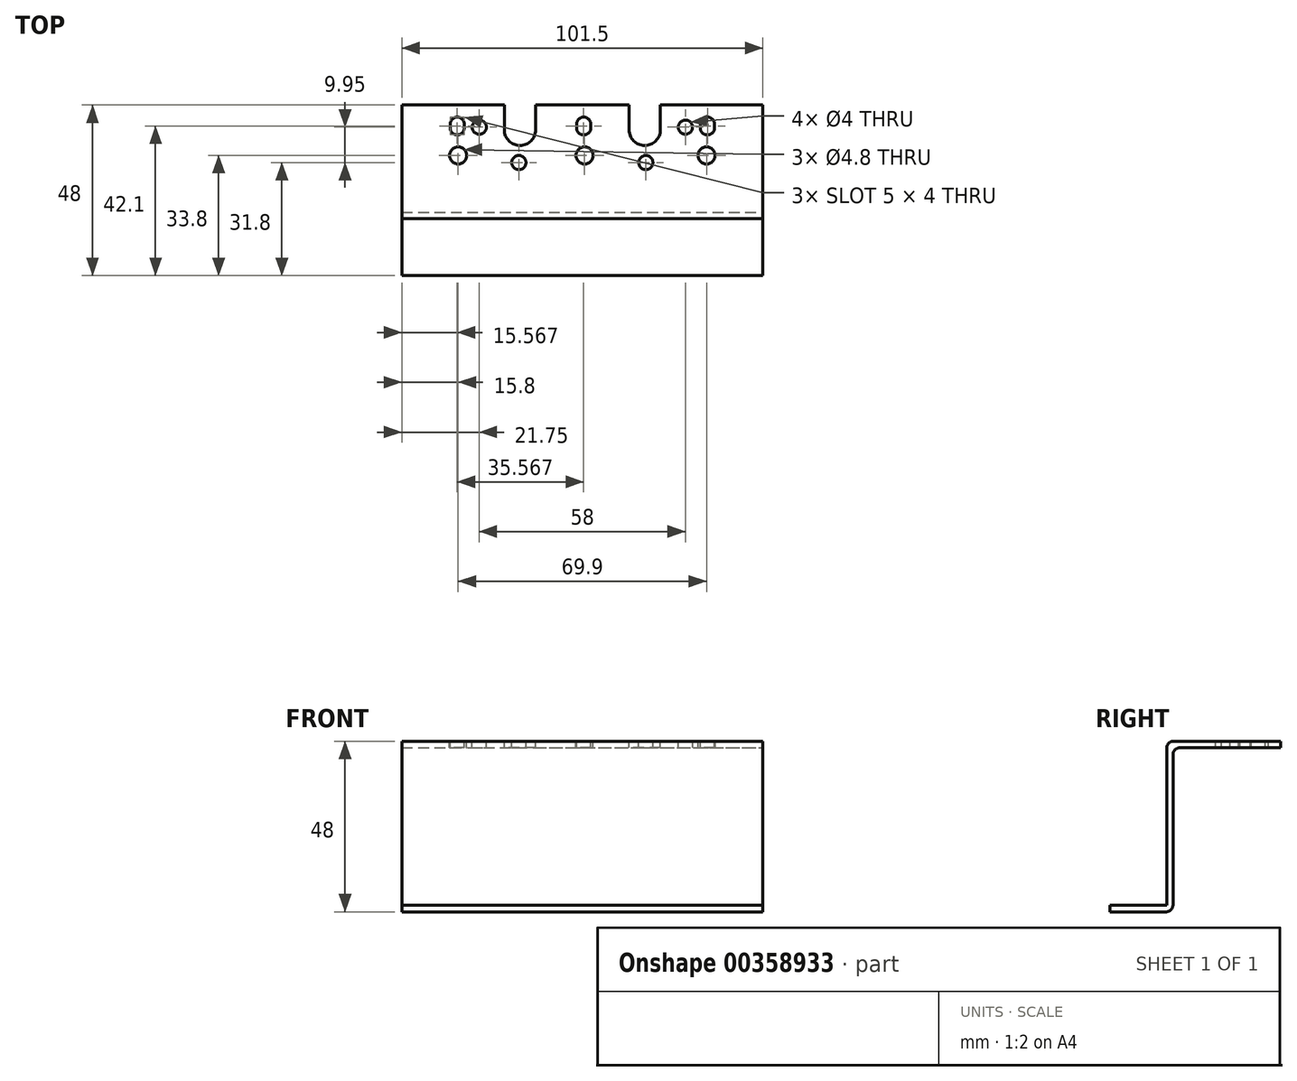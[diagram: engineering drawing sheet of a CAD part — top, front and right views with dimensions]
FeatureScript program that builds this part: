
annotation { "Feature Type Name" : "Feature", "Feature Type Description" : "" }
export const myFeature = defineFeature(function(context is Context, id is Id, definition is map)
    precondition{}
    {
        {
            var Q0;
            Q0=qCreatedBy(makeId("Front.planeOp"),FACE);
            var sketch = newSketch(context, id + "F0", { "sketchPlane" : qUnion([Q0])});
            skLineSegment(sketch, "E0.bottom", {"start": v(0, 0) * mm, "end": v(101.5, 0) * mm});
            skLineSegment(sketch, "E0.top", {"start": v(0, 48) * mm, "end": v(101.5, 48) * mm});
            skLineSegment(sketch, "E0.left", {"start": v(0, 0) * mm, "end": v(0, 48) * mm});
            skLineSegment(sketch, "E0.right", {"start": v(101.5, 0) * mm, "end": v(101.5, 48) * mm});
            skSolve(sketch);
        }
        {
            var Q0;
            Q0 = qSketchRegion(id + "F0", true);
            extrude(context, id + "F1", {"entities" : qUnion([Q0]), "depth" : 1.8 * mm});
        }
        {
            var Q0;
            Q0=makeQuery(id+"F1.opExtrude","CAP_FACE",FACE,{"disambiguationData":[OSD([sQuery(id+"F0.wireOp",EDGE,"E0.bottom"),sQuery(id+"F0.wireOp",EDGE,"E0.top"),sQuery(id+"F0.wireOp",EDGE,"E0.left"),sQuery(id+"F0.wireOp",EDGE,"E0.right")])],"isStart":false});
            var sketch = newSketch(context, id + "F2", { "sketchPlane" : qUnion([Q0])});
            skLineSegment(sketch, "E1.bottom", {"start": v(0, 0) * mm, "end": v(101.5, 0) * mm});
            skLineSegment(sketch, "E1.top", {"start": v(0, 1.8) * mm, "end": v(101.5, 1.8) * mm});
            skLineSegment(sketch, "E1.left", {"start": v(0, 0) * mm, "end": v(0, 1.8) * mm});
            skLineSegment(sketch, "E1.right", {"start": v(101.5, 0) * mm, "end": v(101.5, 1.8) * mm});
            skLineSegment(sketch, "E2.bottom", {"start": v(0, 48) * mm, "end": v(101.5, 48) * mm});
            skLineSegment(sketch, "E2.top", {"start": v(0, 46.2) * mm, "end": v(101.5, 46.2) * mm});
            skLineSegment(sketch, "E2.left", {"start": v(0, 48) * mm, "end": v(0, 46.2) * mm});
            skLineSegment(sketch, "E2.right", {"start": v(101.5, 48) * mm, "end": v(101.5, 46.2) * mm});
            skSolve(sketch);
        }
        {
            var Q0;
            Q0=makeQuery(id+"F2.imprint","IMPRINT",FACE,{"disambiguationData":[TD([[makeQuery(id+"F2.imprint","IMPRINT",EDGE,{"derivedFrom":sQuery(id+"F2.wireOp",EDGE,"E1.bottom")}),1.0]])]});
            extrude(context, id + "F3", {"entities" : qUnion([Q0]), "operationType" : NewBodyOperationType.ADD, "depth" : 16 * mm});
        }
        {
            var Q0;
            Q0=makeQuery(id+"F2.imprint","IMPRINT",FACE,{"disambiguationData":[TD([[makeQuery(id+"F2.imprint","IMPRINT",EDGE,{"derivedFrom":sQuery(id+"F2.wireOp",EDGE,"E2.bottom")}),-1.0]])]});
            extrude(context, id + "F4", {"entities" : qUnion([Q0]), "operationType" : NewBodyOperationType.ADD, "oppositeDirection" : true, "depth" : 32 * mm});
        }
        {
            var Q0;
            Q0=makeQuery(id+"F1.opExtrude","CAP_EDGE",EDGE,{"disambiguationData":[OSD([sQuery(id+"F0.wireOp",EDGE,"E0.top")])],"isStart":false});
            var Q1;
            Q1=makeQuery(id+"F3.opExtrude","CAP_EDGE",EDGE,{"disambiguationData":[OSD([sQuery(id+"F2.wireOp",EDGE,"E1.top")])],"isStart":true});
            var Q2;
            Q2=makeQuery(id+"F4.boolean.opBoolean","INTERSECT",EDGE,{"derivedFrom":[makeQuery(id+"F1.opExtrude","CAP_FACE",FACE,{"disambiguationData":[OSD([sQuery(id+"F0.wireOp",EDGE,"E0.bottom"),sQuery(id+"F0.wireOp",EDGE,"E0.top"),sQuery(id+"F0.wireOp",EDGE,"E0.left"),sQuery(id+"F0.wireOp",EDGE,"E0.right")])],"isStart":true}),makeQuery(id+"F4.opExtrude","SWEPT_FACE",FACE,{"disambiguationData":[OSD([sQuery(id+"F2.wireOp",EDGE,"E2.top")])]})]});
            var Q3;
            Q3=makeQuery(id+"F1.opExtrude","CAP_EDGE",EDGE,{"disambiguationData":[OSD([sQuery(id+"F0.wireOp",EDGE,"E0.bottom")])],"isStart":true});
            fillet(context, id + "F5", {"entities" : qUnion([Q0, Q1, Q2, Q3]), "radius" : 2 * mm, "tangentPropagation" : true, "allowEdgeOverflow" : false});
        }
        {
            var Q0;
            Q0=makeQuery(id+"F4.boolean.opBoolean","MERGE",FACE,{"derivedFrom":[makeQuery(id+"F1.opExtrude","SWEPT_FACE",FACE,{"disambiguationData":[OSD([sQuery(id+"F0.wireOp",EDGE,"E0.top")])]}),makeQuery(id+"F4.opExtrude","SWEPT_FACE",FACE,{"disambiguationData":[OSD([sQuery(id+"F2.wireOp",EDGE,"E2.bottom")])]})]});
            var sketch = newSketch(context, id + "F6", { "sketchPlane" : qUnion([Q0])});
            skLineSegment(sketch, "E3", {"start": v(28.8, 30.2) * mm, "end": v(28.8, 23.2) * mm});
            skLineSegment(sketch, "E4", {"start": v(37.6, 30.2) * mm, "end": v(37.6, 23.2) * mm});
            skArc(sketch, "E5", {"start": v(28.8, 23.2) * mm, "mid": v(33.2, 18.8) * mm, "end": v(37.6, 23.2) * mm});
            skCircle(sketch, "E6", {"center": v(15.8, 16) * mm, "radius": 2.4 * mm});
            skCircle(sketch, "E7", {"center": v(21.75, 23.95) * mm, "radius": 2 * mm});
            skLineSegment(sketch, "E8", {"start": v(13.57, 24.8) * mm, "end": v(13.57, 23.8) * mm});
            skLineSegment(sketch, "E9", {"start": v(17.57, 24.8) * mm, "end": v(17.57, 23.8) * mm});
            skArc(sketch, "E10", {"start": v(17.57, 24.8) * mm, "mid": v(15.57, 26.8) * mm, "end": v(13.57, 24.8) * mm});
            skArc(sketch, "E11", {"start": v(13.57, 23.8) * mm, "mid": v(15.57, 21.8) * mm, "end": v(17.57, 23.8) * mm});
            skCircle(sketch, "E12", {"center": v(32.9, 14) * mm, "radius": 2 * mm});
            skLineSegment(sketch, "E13.MirrorCS", {"start": v(87.93, 24.8) * mm, "end": v(87.93, 23.8) * mm});
            skLineSegment(sketch, "E14.MirrorCS", {"start": v(83.93, 24.8) * mm, "end": v(83.93, 23.8) * mm});
            skCircle(sketch, "E15.MirrorC", {"center": v(79.75, 23.95) * mm, "radius": 2 * mm});
            skLineSegment(sketch, "E16.MirrorCS", {"start": v(72.7, 30.2) * mm, "end": v(72.7, 23.2) * mm});
            skLineSegment(sketch, "E17.MirrorCS", {"start": v(63.9, 30.2) * mm, "end": v(63.9, 23.2) * mm});
            skArc(sketch, "E18.MirrorCS", {"start": v(83.93, 24.8) * mm, "mid": v(85.93, 26.8) * mm, "end": v(87.93, 24.8) * mm});
            skArc(sketch, "E19.MirrorCS", {"start": v(87.93, 23.8) * mm, "mid": v(85.93, 21.8) * mm, "end": v(83.93, 23.8) * mm});
            skCircle(sketch, "E20.MirrorC", {"center": v(85.7, 16) * mm, "radius": 2.4 * mm});
            skArc(sketch, "E21.MirrorCS", {"start": v(72.7, 23.2) * mm, "mid": v(68.3, 18.8) * mm, "end": v(63.9, 23.2) * mm});
            skCircle(sketch, "E22.MirrorC", {"center": v(68.6, 14) * mm, "radius": 2 * mm});
            skLineSegment(sketch, "E23.MirrorCS", {"start": v(53.13, 24.8) * mm, "end": v(53.13, 23.8) * mm});
            skLineSegment(sketch, "E24.MirrorCS", {"start": v(49.13, 24.8) * mm, "end": v(49.13, 23.8) * mm});
            skArc(sketch, "E25.MirrorCS", {"start": v(53.13, 24.8) * mm, "mid": v(51.13, 26.8) * mm, "end": v(49.13, 24.8) * mm});
            skCircle(sketch, "E26.MirrorC", {"center": v(51.37, 16) * mm, "radius": 2.4 * mm});
            skArc(sketch, "E27.MirrorCS", {"start": v(49.13, 23.8) * mm, "mid": v(51.13, 21.8) * mm, "end": v(53.13, 23.8) * mm});
            skSolve(sketch);
        }
        {
            var Q0;
            Q0 = qSketchRegion(id + "F6", true);
            var Q1;
            {var subQ0=sQuery(id+"F6.wireOp",EDGE,"E3");Q1=makeQuery(id+"F6.imprint","IMPRINT",FACE,{"disambiguationData":[TD([[makeQuery(id+"F6.imprint","IMPRINT",EDGE,{"derivedFrom":subQ0}),1.0]])]});}
            var Q2;
            {var subQ0=sQuery(id+"F6.wireOp",EDGE,"E16.MirrorCS");Q2=makeQuery(id+"F6.imprint","IMPRINT",FACE,{"disambiguationData":[TD([[makeQuery(id+"F6.imprint","IMPRINT",EDGE,{"derivedFrom":subQ0}),-1.0]])]});}
            extrude(context, id + "F7", {"entities" : qUnion([Q0, Q1, Q2]), "operationType" : NewBodyOperationType.REMOVE, "endBound" : BoundingType.THROUGH_ALL, "oppositeDirection" : true, "depth" : 25 * mm});
        }
    });
